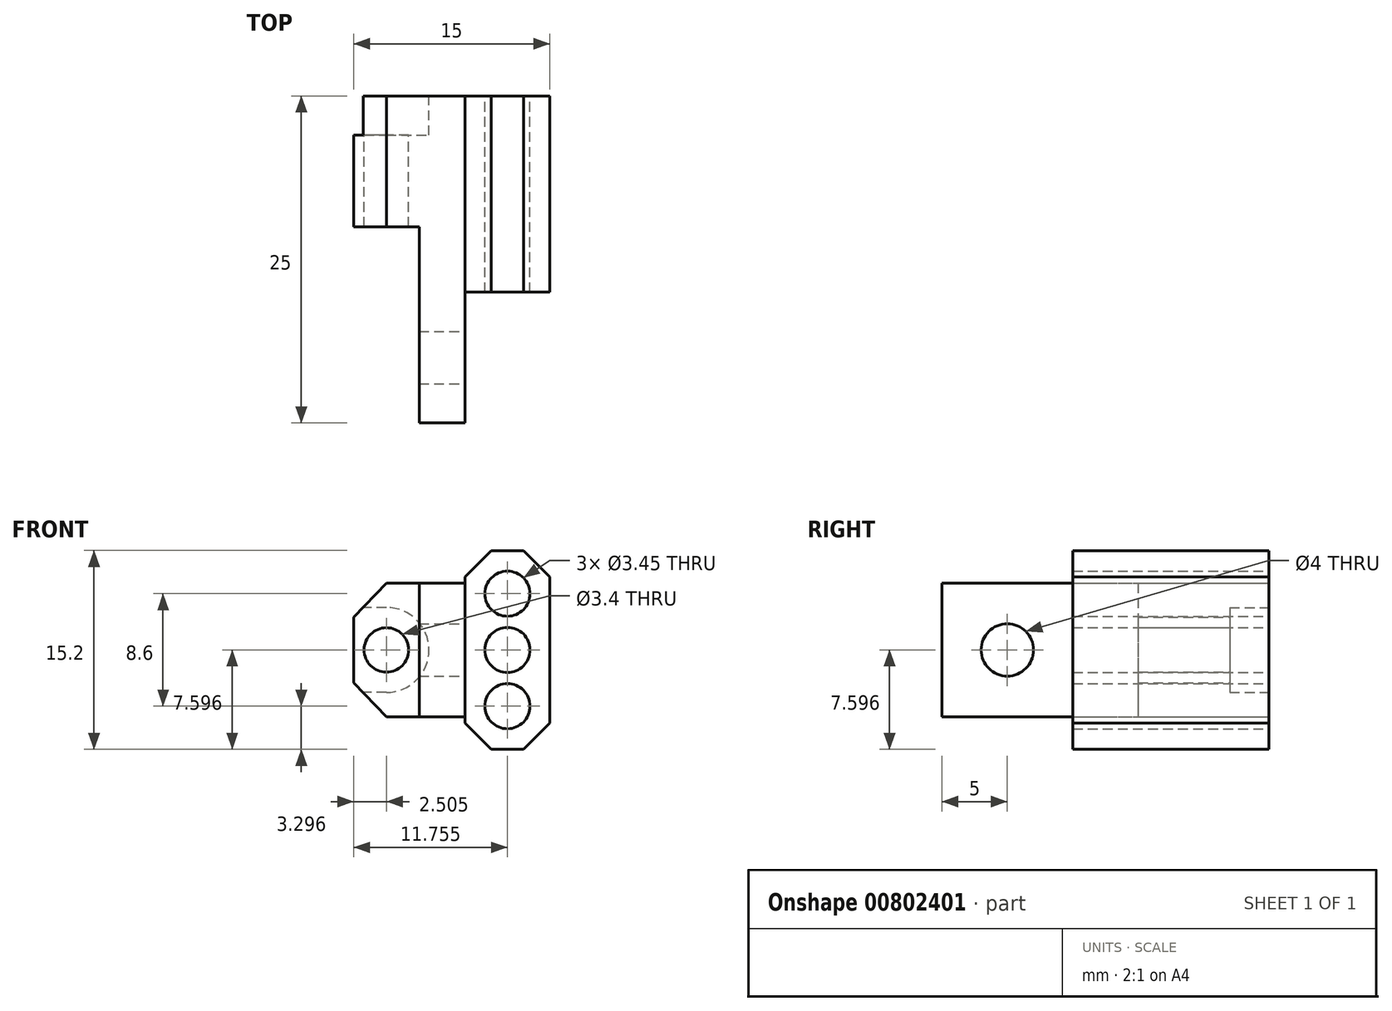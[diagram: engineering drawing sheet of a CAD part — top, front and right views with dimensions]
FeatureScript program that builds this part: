
annotation { "Feature Type Name" : "Feature", "Feature Type Description" : "" }
export const myFeature = defineFeature(function(context is Context, id is Id, definition is map)
    precondition{}
    {
        {
            var Q0;
            Q0=qCreatedBy(makeId("Front.planeOp"),FACE);
            var sketch = newSketch(context, id + "F0", { "sketchPlane" : qUnion([Q0])});
            skLineSegment(sketch, "E0.bottom", {"start": v(-1.3, 33.8) * mm, "end": v(1.2, 33.8) * mm});
            skLineSegment(sketch, "E0.top", {"start": v(-1.3, 18.6) * mm, "end": v(1.2, 18.6) * mm});
            skLineSegment(sketch, "E0.left", {"start": v(-3.3, 31.8) * mm, "end": v(-3.3, 20.6) * mm});
            skLineSegment(sketch, "E0.right", {"start": v(3.2, 31.8) * mm, "end": v(3.2, 20.6) * mm});
            skLineSegment(sketch, "E1", {"start": v(-3.3, 31.8) * mm, "end": v(-1.3, 33.8) * mm});
            skLineSegment(sketch, "E2", {"start": v(1.2, 33.8) * mm, "end": v(3.2, 31.8) * mm});
            skLineSegment(sketch, "E3", {"start": v(-3.3, 20.6) * mm, "end": v(-1.3, 18.6) * mm});
            skLineSegment(sketch, "E4", {"start": v(1.2, 18.6) * mm, "end": v(3.2, 20.6) * mm});
            skPoint(sketch, "E5.orphan", {"position": v(3.2, 33.8) * mm});
            skPoint(sketch, "E6.orphan", {"position": v(-3.3, 18.6) * mm});
            skPoint(sketch, "E7.orphan", {"position": v(3.2, 18.6) * mm});
            skCircle(sketch, "E8", {"center": v(-0.06, 30.5) * mm, "radius": 1.73 * mm});
            skPoint(sketch, "E8.centerSnap0", {"position": v(-0.06, 33.8) * mm});
            skCircle(sketch, "E9", {"center": v(-0.06, 26.2) * mm, "radius": 1.73 * mm});
            skCircle(sketch, "E10", {"center": v(-0.06, 21.9) * mm, "radius": 1.73 * mm});
            skLineSegment(sketch, "E11", {"start": v(-3.3, 31.3) * mm, "end": v(-9.3, 31.3) * mm});
            skLineSegment(sketch, "E12", {"start": v(-9.3, 31.3) * mm, "end": v(-11.8, 28.7) * mm});
            skLineSegment(sketch, "E13", {"start": v(-11.8, 28.7) * mm, "end": v(-11.8, 23.7) * mm});
            skLineSegment(sketch, "E14", {"start": v(-11.8, 23.7) * mm, "end": v(-9.3, 21.1) * mm});
            skLineSegment(sketch, "E15", {"start": v(-9.3, 21.1) * mm, "end": v(-3.3, 21.1) * mm});
            skCircle(sketch, "E16", {"center": v(-9.3, 26.2) * mm, "radius": 1.7 * mm});
            skPoint(sketch, "E16.centerSnap0", {"position": v(-11.8, 26.2) * mm});
            skSolve(sketch);
        }
        {
            var Q0;
            {var subQ0=sQuery(id+"F0.wireOp",EDGE,"E11");Q0=makeQuery(id+"F0.imprint","IMPRINT",FACE,{"disambiguationData":[TD([[makeQuery(id+"F0.imprint","IMPRINT",EDGE,{"derivedFrom":subQ0}),1.0]])]});}
            var Q1;
            Q1=makeQuery(id+"F0.imprint","IMPRINT",FACE,{"disambiguationData":[TD([[makeQuery(id+"F0.imprint","IMPRINT",EDGE,{"derivedFrom":sQuery(id+"F0.wireOp",EDGE,"E0.bottom")}),-1.0]])]});
            extrude(context, id + "F1", {"entities" : qUnion([Q0, Q1]), "depth" : 15 * mm, "offsetDistance" : 25 * mm});
        }
        {
            var Q0;
            Q0=makeQuery(id+"F1.opExtrude","CAP_FACE",FACE,{"disambiguationData":[OSD([sQuery(id+"F0.wireOp",EDGE,"E0.bottom"),sQuery(id+"F0.wireOp",EDGE,"E0.left"),sQuery(id+"F0.wireOp",EDGE,"E0.right"),sQuery(id+"F0.wireOp",EDGE,"E1"),sQuery(id+"F0.wireOp",EDGE,"E2"),sQuery(id+"F0.wireOp",EDGE,"E3"),sQuery(id+"F0.wireOp",EDGE,"E0.top"),sQuery(id+"F0.wireOp",EDGE,"E4"),sQuery(id+"F0.wireOp",EDGE,"E8"),sQuery(id+"F0.wireOp",EDGE,"E9"),sQuery(id+"F0.wireOp",EDGE,"E10"),sQuery(id+"F0.wireOp",EDGE,"E11"),sQuery(id+"F0.wireOp",EDGE,"E12"),sQuery(id+"F0.wireOp",EDGE,"E13"),sQuery(id+"F0.wireOp",EDGE,"E14"),sQuery(id+"F0.wireOp",EDGE,"E15"),sQuery(id+"F0.wireOp",EDGE,"E16")])],"isStart":false});
            var sketch = newSketch(context, id + "F2", { "sketchPlane" : qUnion([Q0])});
            skLineSegment(sketch, "E17", {"start": v(-6.8, 31.3) * mm, "end": v(-6.8, 21.1) * mm});
            skLineSegment(sketch, "E18", {"start": v(-6.8, 21.1) * mm, "end": v(-3.3, 21.1) * mm});
            skLineSegment(sketch, "E19", {"start": v(-3.3, 21.1) * mm, "end": v(-3.3, 31.3) * mm});
            skLineSegment(sketch, "E20", {"start": v(-3.3, 31.3) * mm, "end": v(-6.8, 31.3) * mm});
            skSolve(sketch);
        }
        {
            var Q0;
            Q0=makeQuery(id+"F2.imprint","IMPRINT",FACE,{"disambiguationData":[TD([[makeQuery(id+"F2.imprint","IMPRINT",EDGE,{"derivedFrom":sQuery(id+"F2.wireOp",EDGE,"E17")}),1.0]])]});
            extrude(context, id + "F3", {"entities" : qUnion([Q0]), "operationType" : NewBodyOperationType.ADD, "depth" : 10 * mm, "offsetDistance" : 25 * mm});
        }
        {
            var Q0;
            {var subQ0=sQuery(id+"F0.wireOp",EDGE,"E14");var subQ1=sQuery(id+"F0.wireOp",EDGE,"E13");var subQ2=sQuery(id+"F0.wireOp",EDGE,"E12");var subQ3=sQuery(id+"F0.wireOp",EDGE,"E11");var subQ4=sQuery(id+"F0.wireOp",EDGE,"E15");var subQ5=sQuery(id+"F0.wireOp",EDGE,"E16");Q0=makeQuery(id+"F3.boolean.opBoolean","SPLIT",FACE,{"disambiguationData":[TD([makeQuery(id+"F1.opExtrude","SWEPT_FACE",FACE,{"disambiguationData":[OSD([subQ2])]})])],"derivedFrom":makeQuery(id+"F1.opExtrude","CAP_FACE",FACE,{"disambiguationData":[OSD([sQuery(id+"F0.wireOp",EDGE,"E0.bottom"),sQuery(id+"F0.wireOp",EDGE,"E0.left"),sQuery(id+"F0.wireOp",EDGE,"E0.right"),sQuery(id+"F0.wireOp",EDGE,"E1"),sQuery(id+"F0.wireOp",EDGE,"E2"),sQuery(id+"F0.wireOp",EDGE,"E3"),sQuery(id+"F0.wireOp",EDGE,"E0.top"),sQuery(id+"F0.wireOp",EDGE,"E4"),sQuery(id+"F0.wireOp",EDGE,"E8"),sQuery(id+"F0.wireOp",EDGE,"E9"),sQuery(id+"F0.wireOp",EDGE,"E10"),subQ3,subQ2,subQ1,subQ0,subQ4,subQ5])],"isStart":false})});}
            var sketch = newSketch(context, id + "F4", { "sketchPlane" : qUnion([Q0])});
            skLineSegment(sketch, "E21", {"start": v(-6.8, 31.3) * mm, "end": v(-9.3, 31.3) * mm});
            skLineSegment(sketch, "E22", {"start": v(-9.3, 31.3) * mm, "end": v(-11.8, 28.7) * mm});
            skLineSegment(sketch, "E23", {"start": v(-11.8, 28.7) * mm, "end": v(-11.8, 23.7) * mm});
            skLineSegment(sketch, "E24", {"start": v(-11.8, 23.7) * mm, "end": v(-9.3, 21.1) * mm});
            skLineSegment(sketch, "E25", {"start": v(-9.3, 21.1) * mm, "end": v(-6.8, 21.1) * mm});
            skLineSegment(sketch, "E26", {"start": v(-6.8, 21.1) * mm, "end": v(-6.8, 31.3) * mm});
            skCircle(sketch, "E27", {"center": v(-9.3, 26.2) * mm, "radius": 1.7 * mm});
            skSolve(sketch);
        }
        {
            var Q0;
            Q0=makeQuery(id+"F4.imprint","IMPRINT",FACE,{"disambiguationData":[TD([[makeQuery(id+"F4.imprint","IMPRINT",EDGE,{"derivedFrom":sQuery(id+"F4.wireOp",EDGE,"E21")}),1.0]])]});
            extrude(context, id + "F5", {"entities" : qUnion([Q0]), "operationType" : NewBodyOperationType.REMOVE, "oppositeDirection" : true, "depth" : 5 * mm, "offsetDistance" : 25 * mm});
        }
        {
            var Q0;
            Q0=makeQuery(id+"F3.opExtrude","SWEPT_FACE",FACE,{"disambiguationData":[OSD([sQuery(id+"F2.wireOp",EDGE,"E19")])]});
            var sketch = newSketch(context, id + "F6", { "sketchPlane" : qUnion([Q0])});
            skLineSegment(sketch, "E28.bottom", {"start": v(-25, 21.1) * mm, "end": v(-15, 21.1) * mm});
            skLineSegment(sketch, "E28.top", {"start": v(-25, 31.3) * mm, "end": v(-15, 31.3) * mm});
            skLineSegment(sketch, "E28.left", {"start": v(-25, 21.1) * mm, "end": v(-25, 31.3) * mm});
            skLineSegment(sketch, "E28.right", {"start": v(-15, 21.1) * mm, "end": v(-15, 31.3) * mm});
            skCircle(sketch, "E29", {"center": v(-20, 26.2) * mm, "radius": 2 * mm});
            skPoint(sketch, "E29.centerSnap0", {"position": v(-25, 26.2) * mm});
            skSolve(sketch);
        }
        {
            var Q0;
            Q0=makeQuery(id+"F6.imprint","IMPRINT",FACE,{"disambiguationData":[TD([[makeQuery(id+"F6.imprint","IMPRINT",EDGE,{"derivedFrom":sQuery(id+"F6.wireOp",EDGE,"E29")}),1.0]])]});
            extrude(context, id + "F7", {"entities" : qUnion([Q0]), "operationType" : NewBodyOperationType.REMOVE, "oppositeDirection" : true, "depth" : 25 * mm, "offsetDistance" : 25 * mm});
        }
        {
            var Q0;
            Q0=makeQuery(id+"F1.opExtrude","CAP_FACE",FACE,{"disambiguationData":[OSD([sQuery(id+"F0.wireOp",EDGE,"E0.bottom"),sQuery(id+"F0.wireOp",EDGE,"E0.left"),sQuery(id+"F0.wireOp",EDGE,"E0.right"),sQuery(id+"F0.wireOp",EDGE,"E1"),sQuery(id+"F0.wireOp",EDGE,"E2"),sQuery(id+"F0.wireOp",EDGE,"E3"),sQuery(id+"F0.wireOp",EDGE,"E0.top"),sQuery(id+"F0.wireOp",EDGE,"E4"),sQuery(id+"F0.wireOp",EDGE,"E8"),sQuery(id+"F0.wireOp",EDGE,"E9"),sQuery(id+"F0.wireOp",EDGE,"E10"),sQuery(id+"F0.wireOp",EDGE,"E11"),sQuery(id+"F0.wireOp",EDGE,"E12"),sQuery(id+"F0.wireOp",EDGE,"E13"),sQuery(id+"F0.wireOp",EDGE,"E14"),sQuery(id+"F0.wireOp",EDGE,"E15"),sQuery(id+"F0.wireOp",EDGE,"E16")])],"isStart":true});
            var sketch = newSketch(context, id + "F8", { "sketchPlane" : qUnion([Q0])});
            skArc(sketch, "E30", {"start": v(9.3, 29.45) * mm, "mid": v(6.06, 26.2) * mm, "end": v(9.3, 22.95) * mm});
            skLineSegment(sketch, "E31", {"start": v(9.3, 29.45) * mm, "end": v(11.08, 29.45) * mm});
            skLineSegment(sketch, "E32", {"start": v(9.3, 22.95) * mm, "end": v(11.08, 22.95) * mm});
            skLineSegment(sketch, "E33", {"start": v(11.08, 29.45) * mm, "end": v(11.8, 28.7) * mm});
            skLineSegment(sketch, "E34", {"start": v(11.8, 28.7) * mm, "end": v(11.8, 23.7) * mm});
            skLineSegment(sketch, "E35", {"start": v(11.8, 23.7) * mm, "end": v(11.08, 22.95) * mm});
            skPoint(sketch, "E36.orphan", {"position": v(14.1, 29.45) * mm});
            skPoint(sketch, "E37.orphan", {"position": v(14.1, 22.95) * mm});
            skSolve(sketch);
        }
        {
            var Q0;
            Q0 = qSketchRegion(id + "F8", true);
            extrude(context, id + "F9", {"entities" : qUnion([Q0]), "operationType" : NewBodyOperationType.REMOVE, "oppositeDirection" : true, "depth" : 3 * mm, "offsetDistance" : 25 * mm});
        }
    });
